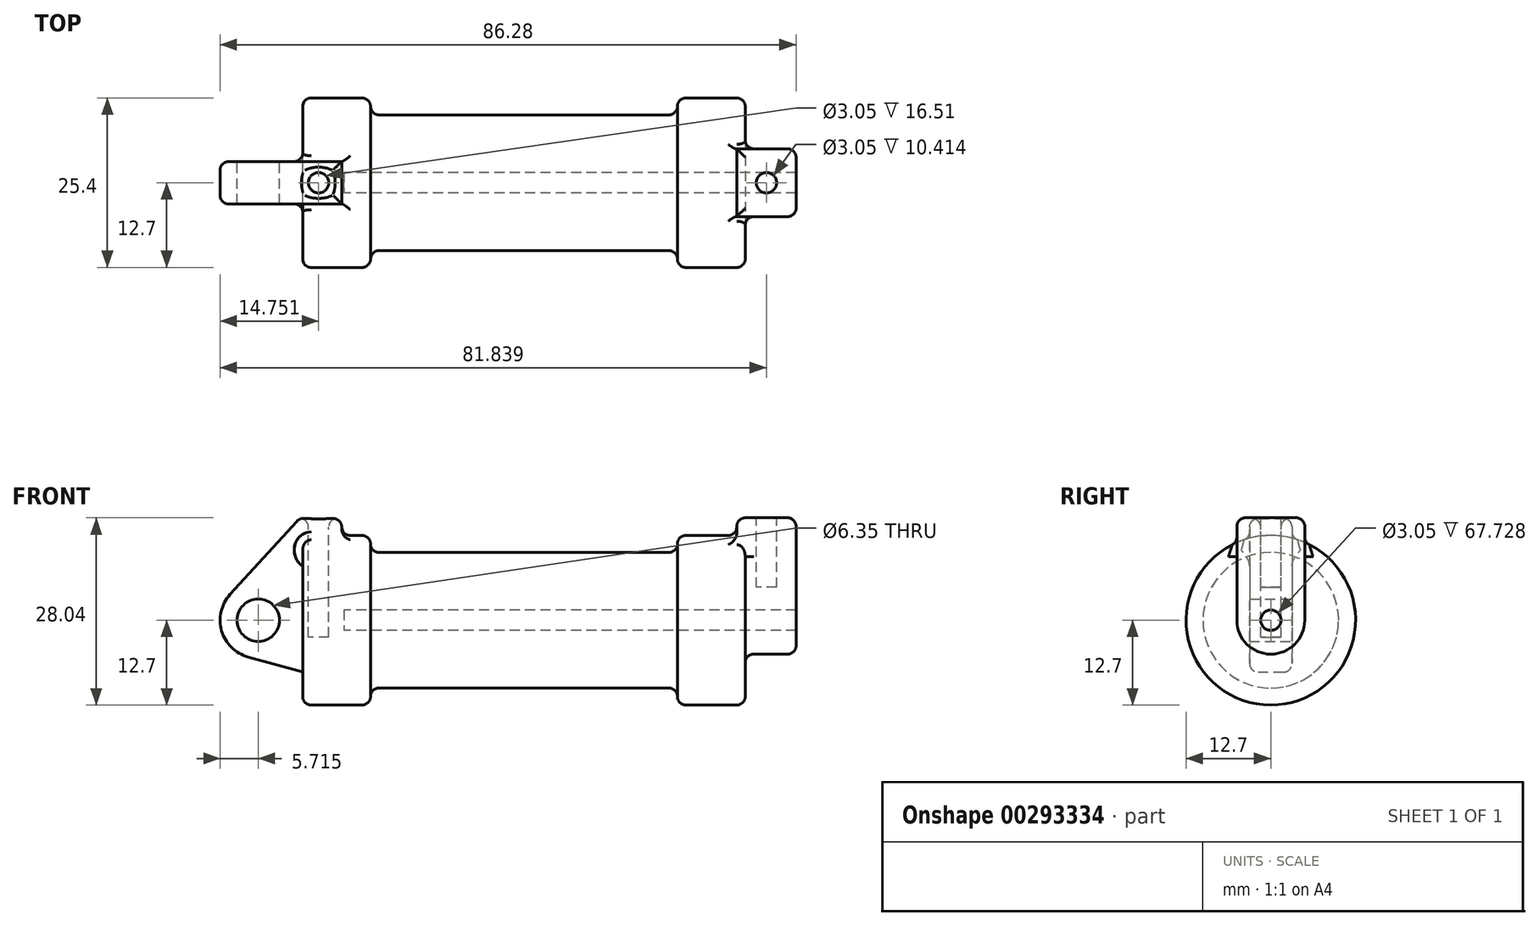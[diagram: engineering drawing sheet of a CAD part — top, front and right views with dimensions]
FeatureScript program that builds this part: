
annotation { "Feature Type Name" : "Feature", "Feature Type Description" : "" }
export const myFeature = defineFeature(function(context is Context, id is Id, definition is map)
    precondition{}
    {
        {
            var Q0;
            Q0=qCreatedBy(makeId("Front.planeOp"),FACE);
            var sketch = newSketch(context, id + "F0", { "sketchPlane" : qUnion([Q0])});
            skLineSegment(sketch, "E0", {"start": v(0, 0) * mm, "end": v(0, 12.7) * mm});
            skLineSegment(sketch, "E1", {"start": v(0, 12.7) * mm, "end": v(10.16, 12.7) * mm});
            skLineSegment(sketch, "E2", {"start": v(10.16, 12.7) * mm, "end": v(10.16, 10.16) * mm});
            skLineSegment(sketch, "E3", {"start": v(10.16, 10.16) * mm, "end": v(56.13, 10.16) * mm});
            skLineSegment(sketch, "E4", {"start": v(56.13, 10.16) * mm, "end": v(56.13, 12.7) * mm});
            skLineSegment(sketch, "E5", {"start": v(56.13, 12.7) * mm, "end": v(66.3, 12.7) * mm});
            skLineSegment(sketch, "E6", {"start": v(66.3, 12.7) * mm, "end": v(66.3, 0) * mm});
            skLineSegment(sketch, "E7", {"start": v(66.3, 0) * mm, "end": v(0, 0) * mm});
            skLineSegment(sketch, "E8", {"start": v(5.84, 15.24) * mm, "end": v(-0.5, 15.24) * mm});
            skLineSegment(sketch, "E9", {"start": v(-0.5, 15.24) * mm, "end": v(-10.88, 3.85) * mm});
            skLineSegment(sketch, "E10", {"start": v(0, 0) * mm, "end": v(-6.65, 0) * mm});
            skCircle(sketch, "E11", {"center": v(-6.65, 0) * mm, "radius": 5.72 * mm});
            skCircle(sketch, "E12", {"center": v(-6.65, 0) * mm, "radius": 3.18 * mm});
            skLineSegment(sketch, "E13", {"start": v(5.84, 15.24) * mm, "end": v(5.84, -9.4) * mm});
            skLineSegment(sketch, "E14", {"start": v(5.84, -9.4) * mm, "end": v(-8.18, -5.5) * mm});
            skSolve(sketch);
        }
        {
            var Q0;
            {var subQ0=sQuery(id+"F0.wireOp",EDGE,"E2");Q0=makeQuery(id+"F0.imprint","IMPRINT",FACE,{"disambiguationData":[TD([[makeQuery(id+"F0.imprint","IMPRINT",EDGE,{"derivedFrom":subQ0}),-1.0]])]});}
            var Q1;
            {var subQ0=sQuery(id+"F0.wireOp",EDGE,"E0");Q1=makeQuery(id+"F0.imprint","IMPRINT",FACE,{"disambiguationData":[TD([[makeQuery(id+"F0.imprint","IMPRINT",EDGE,{"derivedFrom":subQ0}),-1.0]])]});}
            var Q2;
            Q2=sQuery(id+"F0.wireOp",EDGE,"E7");
            revolve(context, id + "F1", {"entities" : qUnion([Q0, Q1]), "axis" : qUnion([Q2]), "revolveType" : RevolveType.FULL});
        }
        {
            var Q0;
            {var subQ1=sQuery(id+"F0.wireOp",EDGE,"E0");Q0=makeQuery(id+"F0.imprint","IMPRINT",FACE,{"disambiguationData":[TD([[makeQuery(id+"F0.imprint","IMPRINT",EDGE,{"derivedFrom":subQ1}),1.0]])]});}
            var Q1;
            {var subQ0=sQuery(id+"F0.wireOp",EDGE,"E14");Q1=makeQuery(id+"F0.imprint","IMPRINT",FACE,{"disambiguationData":[TD([[makeQuery(id+"F0.imprint","IMPRINT",EDGE,{"derivedFrom":subQ0}),-1.0]])]});}
            var Q2;
            {var subQ5=sQuery(id+"F0.wireOp",EDGE,"E12");Q2=makeQuery(id+"F0.imprint","IMPRINT",FACE,{"disambiguationData":[TD([[makeQuery(id+"F0.imprint","IMPRINT",EDGE,{"derivedFrom":subQ5}),-1.0]])]});}
            var Q3;
            {var subQ0=sQuery(id+"F0.wireOp",EDGE,"E0");Q3=makeQuery(id+"F0.imprint","IMPRINT",FACE,{"disambiguationData":[TD([[makeQuery(id+"F0.imprint","IMPRINT",EDGE,{"derivedFrom":subQ0}),-1.0]])]});}
            extrude(context, id + "F2", {"entities" : qUnion([Q0, Q1, Q2, Q3]), "operationType" : NewBodyOperationType.ADD, "endBound" : BoundingType.SYMMETRIC, "depth" : 6.35 * mm});
        }
        {
            var Q0;
            Q0=makeQuery(id+"F1.opRevolve","SWEPT_FACE",FACE,{"disambiguationData":[OSD([sQuery(id+"F0.wireOp",EDGE,"E6")])]});
            var sketch = newSketch(context, id + "F3", { "sketchPlane" : qUnion([Q0])});
            skCircle(sketch, "E15", {"center": v(0, 0) * mm, "radius": 5.08 * mm});
            skCircle(sketch, "E16", {"center": v(0, 0) * mm, "radius": 1.52 * mm});
            skLineSegment(sketch, "E17", {"start": v(-5.08, 0) * mm, "end": v(-5.08, 15.34) * mm});
            skLineSegment(sketch, "E18", {"start": v(5.08, 0) * mm, "end": v(5.08, 15.34) * mm});
            skLineSegment(sketch, "E19", {"start": v(-5.08, 15.34) * mm, "end": v(5.08, 15.34) * mm});
            skSolve(sketch);
        }
        {
            var Q0;
            Q0 = qSketchRegion(id + "F3", true);
            extrude(context, id + "F4", {"entities" : qUnion([Q0]), "operationType" : NewBodyOperationType.ADD, "depth" : 7.62 * mm, "hasSecondDirection" : true, "secondDirectionOppositeDirection" : true, "secondDirectionDepth" : 1.27 * mm});
        }
        {
            var Q0;
            Q0=makeQuery(id+"F4.opExtrude","SWEPT_FACE",FACE,{"disambiguationData":[OSD([sQuery(id+"F3.wireOp",EDGE,"E19")])]});
            var sketch = newSketch(context, id + "F5", { "sketchPlane" : qUnion([Q0])});
            skCircle(sketch, "E20", {"center": v(69.47, 0) * mm, "radius": 1.52 * mm});
            skSolve(sketch);
        }
        {
            var Q0;
            Q0=makeQuery(id+"F2.opExtrude","SWEPT_FACE",FACE,{"disambiguationData":[OSD([sQuery(id+"F0.wireOp",EDGE,"E8")])]});
            var sketch = newSketch(context, id + "F6", { "sketchPlane" : qUnion([Q0])});
            skCircle(sketch, "E21", {"center": v(2.38, 0) * mm, "radius": 1.52 * mm});
            skSolve(sketch);
        }
        {
            var Q0;
            Q0=makeQuery(id+"F4.boolean.opBoolean","SPLIT",FACE,{"disambiguationData":[TD([makeQuery(id+"F4.opExtrude","SWEPT_FACE",FACE,{"disambiguationData":[OSD([sQuery(id+"F3.wireOp",EDGE,"E16")])]})])],"derivedFrom":makeQuery(id+"F1.opRevolve","SWEPT_FACE",FACE,{"disambiguationData":[OSD([sQuery(id+"F0.wireOp",EDGE,"E6")])]})});
            extrude(context, id + "F7", {"entities" : qUnion([Q0]), "operationType" : NewBodyOperationType.REMOVE, "oppositeDirection" : true, "depth" : 60.1 * mm});
        }
        {
            var Q0;
            Q0=makeQuery(id+"F6.imprint","IMPRINT",FACE,{"disambiguationData":[TD([[makeQuery(id+"F6.imprint","IMPRINT",EDGE,{"derivedFrom":sQuery(id+"F6.wireOp",EDGE,"E21")}),1.0]])]});
            var Q1;
            Q1=sQuery(id+"F6.wireOp",EDGE,"E21");
            extrude(context, id + "F8", {"entities" : qUnion([Q0]), "operationType" : NewBodyOperationType.REMOVE, "surfaceEntities" : qUnion([Q1]), "oppositeDirection" : true, "depth" : 17.78 * mm});
        }
        {
            var Q0;
            Q0=makeQuery(id+"F5.imprint","IMPRINT",FACE,{"disambiguationData":[TD([[makeQuery(id+"F5.imprint","IMPRINT",EDGE,{"derivedFrom":sQuery(id+"F5.wireOp",EDGE,"E20")}),1.0]])]});
            var Q1;
            Q1=sQuery(id+"F5.wireOp",EDGE,"E20");
            extrude(context, id + "F9", {"entities" : qUnion([Q0]), "operationType" : NewBodyOperationType.REMOVE, "surfaceEntities" : qUnion([Q1]), "oppositeDirection" : true, "depth" : 10.4 * mm});
        }
        {
            var Q0;
            Q0=makeQuery(id+"F2.boolean.opBoolean","INTERSECT",EDGE,{"derivedFrom":[makeQuery(id+"F1.opRevolve","SWEPT_FACE",FACE,{"disambiguationData":[OSD([sQuery(id+"F0.wireOp",EDGE,"E1")])]}),makeQuery(id+"F2.opExtrude","SWEPT_FACE",FACE,{"disambiguationData":[OSD([sQuery(id+"F0.wireOp",EDGE,"E13")])]})]});
            var Q1;
            Q1=makeQuery(id+"F2.boolean.opBoolean","INTERSECT",EDGE,{"derivedFrom":[makeQuery(id+"F1.opRevolve","SWEPT_FACE",FACE,{"disambiguationData":[OSD([sQuery(id+"F0.wireOp",EDGE,"E1")])]}),makeQuery(id+"F2.opExtrude","CAP_FACE",FACE,{"disambiguationData":[OSD([sQuery(id+"F0.wireOp",EDGE,"E8"),sQuery(id+"F0.wireOp",EDGE,"E9"),sQuery(id+"F0.wireOp",EDGE,"E11"),sQuery(id+"F0.wireOp",EDGE,"E12"),sQuery(id+"F0.wireOp",EDGE,"E13"),sQuery(id+"F0.wireOp",EDGE,"E14")])],"isStart":false})]});
            var Q2;
            Q2=makeQuery(id+"F2.boolean.opBoolean","INTERSECT",EDGE,{"derivedFrom":[makeQuery(id+"F1.opRevolve","SWEPT_FACE",FACE,{"disambiguationData":[OSD([sQuery(id+"F0.wireOp",EDGE,"E1")])]}),makeQuery(id+"F2.opExtrude","CAP_FACE",FACE,{"disambiguationData":[OSD([sQuery(id+"F0.wireOp",EDGE,"E8"),sQuery(id+"F0.wireOp",EDGE,"E9"),sQuery(id+"F0.wireOp",EDGE,"E11"),sQuery(id+"F0.wireOp",EDGE,"E12"),sQuery(id+"F0.wireOp",EDGE,"E13"),sQuery(id+"F0.wireOp",EDGE,"E14")])],"isStart":true})]});
            var Q3;
            Q3=makeQuery(id+"F1.opRevolve","SWEPT_EDGE",EDGE,{"disambiguationData":[OSD([sQuery(id+"F0.wireOp",EDGE,"E0"),sQuery(id+"F0.wireOp",EDGE,"E1")])]});
            var Q4;
            Q4=makeQuery(id+"F2.opExtrude","CAP_EDGE",EDGE,{"disambiguationData":[OSD([sQuery(id+"F0.wireOp",EDGE,"E9")])],"isStart":false});
            var Q5;
            Q5=makeQuery(id+"F2.opExtrude","CAP_EDGE",EDGE,{"disambiguationData":[OSD([sQuery(id+"F0.wireOp",EDGE,"E9")])],"isStart":true});
            var Q6;
            Q6=makeQuery(id+"F2.opExtrude","SWEPT_EDGE",EDGE,{"disambiguationData":[OSD([sQuery(id+"F0.wireOp",EDGE,"E8"),sQuery(id+"F0.wireOp",EDGE,"E13")])]});
            var Q7;
            Q7=makeQuery(id+"F2.opExtrude","CAP_EDGE",EDGE,{"disambiguationData":[OSD([sQuery(id+"F0.wireOp",EDGE,"E8")])],"isStart":false});
            var Q8;
            Q8=makeQuery(id+"F2.opExtrude","SWEPT_EDGE",EDGE,{"disambiguationData":[OSD([sQuery(id+"F0.wireOp",EDGE,"E8"),sQuery(id+"F0.wireOp",EDGE,"E9")])]});
            var Q9;
            Q9=makeQuery(id+"F2.opExtrude","SWEPT_FACE",FACE,{"disambiguationData":[OSD([sQuery(id+"F0.wireOp",EDGE,"E8")])]});
            var Q10;
            Q10=makeQuery(id+"F1.opRevolve","SWEPT_EDGE",EDGE,{"disambiguationData":[OSD([sQuery(id+"F0.wireOp",EDGE,"E1"),sQuery(id+"F0.wireOp",EDGE,"E2")])]});
            var Q11;
            Q11=makeQuery(id+"F1.opRevolve","SWEPT_EDGE",EDGE,{"disambiguationData":[OSD([sQuery(id+"F0.wireOp",EDGE,"E2"),sQuery(id+"F0.wireOp",EDGE,"E3")])]});
            fillet(context, id + "F10", {"entities" : qUnion([Q0, Q1, Q2, Q3, Q4, Q5, Q6, Q7, Q8, Q9, Q10, Q11]), "radius" : 1.27 * mm, "tangentPropagation" : true, "allowEdgeOverflow" : false});
        }
        {
            var Q0;
            Q0=makeQuery(id+"F4.opExtrude","SWEPT_EDGE",EDGE,{"disambiguationData":[OSD([sQuery(id+"F3.wireOp",EDGE,"E18"),sQuery(id+"F3.wireOp",EDGE,"E19")])]});
            var Q1;
            Q1=makeQuery(id+"F4.opExtrude","CAP_EDGE",EDGE,{"disambiguationData":[OSD([sQuery(id+"F3.wireOp",EDGE,"E19")])],"isStart":true});
            var Q2;
            Q2=makeQuery(id+"F4.opExtrude","SWEPT_EDGE",EDGE,{"disambiguationData":[OSD([sQuery(id+"F3.wireOp",EDGE,"E17"),sQuery(id+"F3.wireOp",EDGE,"E19")])]});
            var Q3;
            Q3=makeQuery(id+"F4.opExtrude","CAP_EDGE",EDGE,{"disambiguationData":[OSD([sQuery(id+"F3.wireOp",EDGE,"E19")])],"isStart":false});
            var Q4;
            Q4=makeQuery(id+"F4.boolean.opBoolean","INTERSECT",EDGE,{"derivedFrom":[makeQuery(id+"F1.opRevolve","SWEPT_FACE",FACE,{"disambiguationData":[OSD([sQuery(id+"F0.wireOp",EDGE,"E5")])]}),makeQuery(id+"F4.opExtrude","CAP_FACE",FACE,{"disambiguationData":[OSD([sQuery(id+"F3.wireOp",EDGE,"E15"),sQuery(id+"F3.wireOp",EDGE,"E16"),sQuery(id+"F3.wireOp",EDGE,"E17"),sQuery(id+"F3.wireOp",EDGE,"E18"),sQuery(id+"F3.wireOp",EDGE,"E19")])],"isStart":true})]});
            var Q5;
            Q5=makeQuery(id+"F4.opExtrude","CAP_EDGE",EDGE,{"disambiguationData":[OSD([sQuery(id+"F3.wireOp",EDGE,"E18")])],"isStart":false});
            var Q6;
            Q6=makeQuery(id+"F1.opRevolve","SWEPT_EDGE",EDGE,{"disambiguationData":[OSD([sQuery(id+"F0.wireOp",EDGE,"E4"),sQuery(id+"F0.wireOp",EDGE,"E5")])]});
            var Q7;
            Q7=makeQuery(id+"F1.opRevolve","SWEPT_EDGE",EDGE,{"disambiguationData":[OSD([sQuery(id+"F0.wireOp",EDGE,"E3"),sQuery(id+"F0.wireOp",EDGE,"E4")])]});
            var Q8;
            Q8=makeQuery(id+"F1.opRevolve","SWEPT_EDGE",EDGE,{"disambiguationData":[OSD([sQuery(id+"F0.wireOp",EDGE,"E5"),sQuery(id+"F0.wireOp",EDGE,"E6")])]});
            fillet(context, id + "F11", {"entities" : qUnion([Q0, Q1, Q2, Q3, Q4, Q5, Q6, Q7, Q8]), "radius" : 1.27 * mm, "tangentPropagation" : true, "allowEdgeOverflow" : false});
        }
        {
            var Q0;
            Q0=makeQuery(id+"F11.opFillet","BLEND_EDGE",EDGE,{"blendedFrom":[makeQuery(id+"F1.opRevolve","SWEPT_EDGE",EDGE,{"disambiguationData":[OSD([sQuery(id+"F0.wireOp",EDGE,"E5"),sQuery(id+"F0.wireOp",EDGE,"E6")])]}),makeQuery(id+"F4.opExtrude","SWEPT_FACE",FACE,{"disambiguationData":[OSD([sQuery(id+"F3.wireOp",EDGE,"E17")])]})],"blendedInto":[makeQuery(id+"F4.opExtrude","SWEPT_FACE",FACE,{"disambiguationData":[OSD([sQuery(id+"F3.wireOp",EDGE,"E17")])]})]});
            var Q1;
            Q1=makeQuery(id+"F4.boolean.opBoolean","INTERSECT",EDGE,{"derivedFrom":[makeQuery(id+"F1.opRevolve","SWEPT_FACE",FACE,{"disambiguationData":[OSD([sQuery(id+"F0.wireOp",EDGE,"E6")])]}),makeQuery(id+"F4.opExtrude","SWEPT_FACE",FACE,{"disambiguationData":[OSD([sQuery(id+"F3.wireOp",EDGE,"E17")])]})]});
            fillet(context, id + "F12", {"entities" : qUnion([Q0, Q1]), "radius" : 1.27 * mm, "tangentPropagation" : true, "allowEdgeOverflow" : false});
        }
    });
